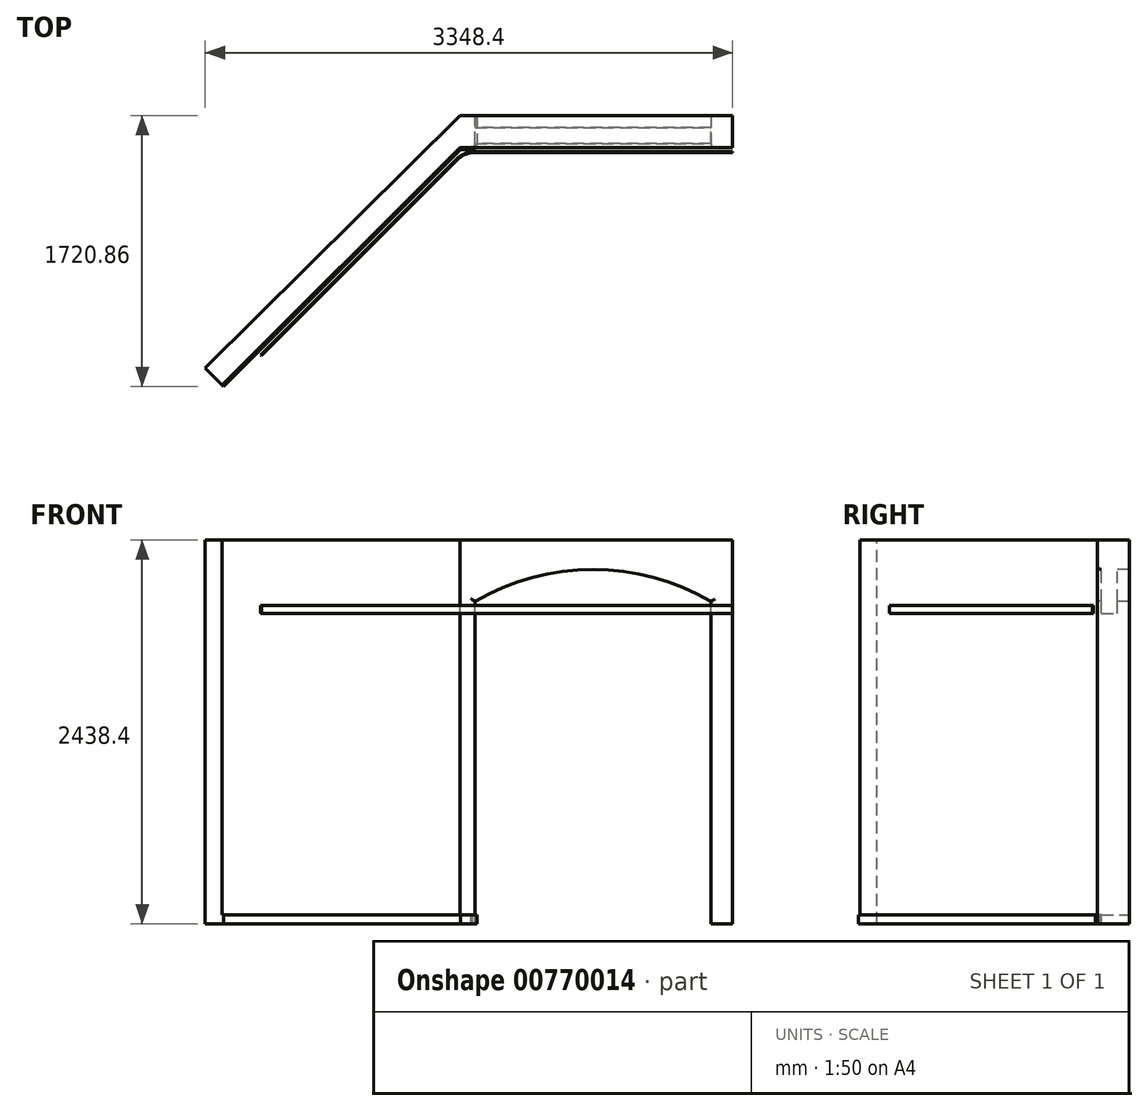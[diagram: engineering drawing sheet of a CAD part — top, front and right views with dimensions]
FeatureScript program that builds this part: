
annotation { "Feature Type Name" : "Feature", "Feature Type Description" : "" }
export const myFeature = defineFeature(function(context is Context, id is Id, definition is map)
    precondition{}
    {
        {
            var Q0;
            Q0=qCreatedBy(makeId("Front.planeOp"),FACE);
            var sketch = newSketch(context, id + "F0", { "sketchPlane" : qUnion([Q0])});
            skLineSegment(sketch, "E0.bottom", {"start": v(0, 0) * mm, "end": v(1498.6, 0) * mm});
            skLineSegment(sketch, "E0.top", {"start": v(0, 1973.26) * mm, "end": v(1498.6, 1973.26) * mm});
            skLineSegment(sketch, "E0.left", {"start": v(0, 0) * mm, "end": v(0, 1973.26) * mm});
            skLineSegment(sketch, "E0.right", {"start": v(1498.6, 0) * mm, "end": v(1498.6, 1973.26) * mm});
            skLineSegment(sketch, "E1", {"start": v(0, 1973.26) * mm, "end": v(0, 2049.46) * mm});
            skLineSegment(sketch, "E2", {"start": v(1498.6, 1973.26) * mm, "end": v(1498.6, 2049.46) * mm});
            skArc(sketch, "E3", {"start": v(1498.6, 2049.46) * mm, "mid": v(749.3, 2251.6) * mm, "end": v(0, 2049.46) * mm});
            skSolve(sketch);
        }
        {
            var Q0;
            Q0=makeQuery(id+"F0.imprint","IMPRINT",FACE,{"disambiguationData":[TD([[makeQuery(id+"F0.imprint","IMPRINT",EDGE,{"derivedFrom":sQuery(id+"F0.wireOp",EDGE,"E0.top")}),1.0]])]});
            extrude(context, id + "F1", {"entities" : qUnion([Q0]), "depth" : 101.6 * mm, "offsetDistance" : 25.4 * mm});
        }
        {
            var Q0;
            Q0=makeQuery(id+"F1.opExtrude","CAP_FACE",FACE,{"disambiguationData":[OSD([sQuery(id+"F0.wireOp",EDGE,"E0.top"),sQuery(id+"F0.wireOp",EDGE,"E1"),sQuery(id+"F0.wireOp",EDGE,"E2"),sQuery(id+"F0.wireOp",EDGE,"E3")])],"isStart":false});
            var sketch = newSketch(context, id + "F2", { "sketchPlane" : qUnion([Q0])});
            skLineSegment(sketch, "E4.bottom", {"start": v(0, 0) * mm, "end": v(1498.6, 0) * mm});
            skLineSegment(sketch, "E4.top", {"start": v(0, 1973.26) * mm, "end": v(1498.6, 1973.26) * mm});
            skLineSegment(sketch, "E4.left", {"start": v(0, 0) * mm, "end": v(0, 1973.26) * mm});
            skLineSegment(sketch, "E4.right", {"start": v(1498.6, 0) * mm, "end": v(1498.6, 1973.26) * mm});
            skLineSegment(sketch, "E5.bottom", {"start": v(-96.84, 0) * mm, "end": v(1635.13, 0) * mm});
            skLineSegment(sketch, "E5.top", {"start": v(-96.84, 2438.4) * mm, "end": v(1635.13, 2438.4) * mm});
            skLineSegment(sketch, "E5.left", {"start": v(-96.84, 0) * mm, "end": v(-96.84, 2438.4) * mm});
            skLineSegment(sketch, "E5.right", {"start": v(1635.13, 0) * mm, "end": v(1635.13, 2438.4) * mm});
            skSolve(sketch);
        }
        {
            var Q0;
            {var subQ3=sQuery(id+"F2.wireOp",EDGE,"E4.left");Q0=makeQuery(id+"F2.imprint","IMPRINT",FACE,{"disambiguationData":[TD([[makeQuery(id+"F2.imprint","IMPRINT",EDGE,{"derivedFrom":subQ3}),1.0]])]});}
            extrude(context, id + "F3", {"entities" : qUnion([Q0]), "oppositeDirection" : true, "depth" : 177.8 * mm, "offsetDistance" : 25.4 * mm});
        }
        {
            var Q0;
            Q0=makeQuery(id+"F3.opExtrude","CAP_FACE",FACE,{"disambiguationData":[OSD([sQuery(id+"F0.wireOp",EDGE,"E1"),sQuery(id+"F0.wireOp",EDGE,"E2"),sQuery(id+"F0.wireOp",EDGE,"E3"),sQuery(id+"F2.wireOp",EDGE,"E4.left"),sQuery(id+"F2.wireOp",EDGE,"E4.right"),sQuery(id+"F2.wireOp",EDGE,"E5.bottom"),sQuery(id+"F2.wireOp",EDGE,"E5.top"),sQuery(id+"F2.wireOp",EDGE,"E5.left"),sQuery(id+"F2.wireOp",EDGE,"E5.right")])],"isStart":true});
            var sketch = newSketch(context, id + "F4", { "sketchPlane" : qUnion([Q0])});
            skSolve(sketch);
        }
        {
            var Q0;
            Q0 = qSketchRegion(id + "F4", true);
            var Q1;
            Q1=makeQuery(id+"F4.imprint","IMPRINT",FACE,{"disambiguationData":[TD([[makeQuery(id+"F4.imprint","IMPRINT",EDGE,{"derivedFrom":makeQuery(id+"F3.opExtrude","CAP_EDGE",EDGE,{"disambiguationData":[OSD([sQuery(id+"F2.wireOp",EDGE,"E5.top")])],"isStart":true})}),-1.0]])]});
            extrude(context, id + "F5", {"entities" : qUnion([Q0, Q1]), "operationType" : NewBodyOperationType.ADD, "depth" : 25.4 * mm, "offsetDistance" : 25.4 * mm});
        }
        {
            var Q0;
            Q0=makeQuery(id+"F5.opExtrude","CAP_EDGE",EDGE,{"disambiguationData":[OSD([sQuery(id+"F0.wireOp",EDGE,"E3")])],"isStart":false});
            var Q1;
            Q1=makeQuery(id+"F5.opExtrude","CAP_EDGE",EDGE,{"disambiguationData":[OSD([sQuery(id+"F0.wireOp",EDGE,"E2"),sQuery(id+"F2.wireOp",EDGE,"E4.right")])],"isStart":false});
            var Q2;
            Q2=makeQuery(id+"F5.opExtrude","CAP_EDGE",EDGE,{"disambiguationData":[OSD([sQuery(id+"F0.wireOp",EDGE,"E1"),sQuery(id+"F2.wireOp",EDGE,"E4.left")])],"isStart":false});
            fillet(context, id + "F6", {"entities" : qUnion([Q0, Q1, Q2]), "radius" : 25.4 * mm, "tangentPropagation" : true, "allowEdgeOverflow" : false});
        }
        {
            var Q0;
            {var subQ0=sQuery(id+"F2.wireOp",EDGE,"E5.top");Q0=makeQuery(id+"F5.boolean.opBoolean","MERGE",FACE,{"derivedFrom":[makeQuery(id+"F3.opExtrude","SWEPT_FACE",FACE,{"disambiguationData":[OSD([subQ0])]}),makeQuery(id+"F5.opExtrude","SWEPT_FACE",FACE,{"disambiguationData":[OSD([subQ0])]})]});}
            var sketch = newSketch(context, id + "F7", { "sketchPlane" : qUnion([Q0])});
            skLineSegment(sketch, "E6", {"start": v(-96.84, -127) * mm, "end": v(-1605.52, -1635.68) * mm});
            skLineSegment(sketch, "E7", {"start": v(-1605.52, -1635.68) * mm, "end": v(-1713.28, -1527.92) * mm});
            skLineSegment(sketch, "E8", {"start": v(-96.84, 76.2) * mm, "end": v(-1713.28, -1527.92) * mm});
            skSolve(sketch);
        }
        {
            var Q0;
            Q0=makeQuery(id+"F7.imprint","IMPRINT",FACE,{"disambiguationData":[TD([[makeQuery(id+"F7.imprint","IMPRINT",EDGE,{"derivedFrom":sQuery(id+"F7.wireOp",EDGE,"E6")}),-1.0]])]});
            extrude(context, id + "F8", {"entities" : qUnion([Q0]), "oppositeDirection" : true, "depth" : 2438.4 * mm, "offsetDistance" : 25.4 * mm});
        }
        {
            var Q0;
            Q0=makeQuery(id+"F8.opExtrude","CAP_FACE",FACE,{"disambiguationData":[OSD([sQuery(id+"F2.wireOp",EDGE,"E5.top"),sQuery(id+"F2.wireOp",EDGE,"E5.left"),sQuery(id+"F7.wireOp",EDGE,"E6"),sQuery(id+"F7.wireOp",EDGE,"E7"),sQuery(id+"F7.wireOp",EDGE,"E8")])],"isStart":false});
            var sketch = newSketch(context, id + "F9", { "sketchPlane" : qUnion([Q0])});
            skLineSegment(sketch, "E9.0", {"start": v(-91.58, 139.7) * mm, "end": v(-1596.54, 1644.66) * mm});
            skLineSegment(sketch, "E9.1", {"start": v(-91.58, 139.7) * mm, "end": v(-25.4, 139.7) * mm});
            skArc(sketch, "E9.2", {"start": v(12.7, 101.6) * mm, "mid": v(1.54, 128.54) * mm, "end": v(-25.4, 139.7) * mm});
            skLineSegment(sketch, "E9.3", {"start": v(12.7, -76.2) * mm, "end": v(12.7, 101.6) * mm});
            skLineSegment(sketch, "E10", {"start": v(12.7, -76.2) * mm, "end": v(0, -76.2) * mm});
            skLineSegment(sketch, "E11", {"start": v(-1596.54, 1644.66) * mm, "end": v(-1605.52, 1635.68) * mm});
            skLineSegment(sketch, "E12", {"start": v(-1605.52, 1635.68) * mm, "end": v(-96.84, 127) * mm});
            skLineSegment(sketch, "E13", {"start": v(-96.84, 127) * mm, "end": v(-20.16, 127) * mm});
            skLineSegment(sketch, "E14", {"start": v(-20.16, 127) * mm, "end": v(0, 106.84) * mm});
            skLineSegment(sketch, "E15", {"start": v(0, 106.84) * mm, "end": v(0, -76.2) * mm});
            skSolve(sketch);
        }
        {
            var Q0;
            Q0=makeQuery(id+"F9.imprint","IMPRINT",FACE,{"disambiguationData":[TD([[makeQuery(id+"F9.imprint","IMPRINT",EDGE,{"derivedFrom":sQuery(id+"F9.wireOp",EDGE,"E9.0")}),1.0]])]});
            extrude(context, id + "F10", {"entities" : qUnion([Q0]), "operationType" : NewBodyOperationType.ADD, "oppositeDirection" : true, "depth" : 57.15 * mm, "offsetDistance" : 25.4 * mm});
        }
        {
            var Q0;
            Q0=makeQuery(id+"F1.opExtrude","SWEPT_FACE",FACE,{"disambiguationData":[OSD([sQuery(id+"F0.wireOp",EDGE,"E0.top")])]});
            var sketch = newSketch(context, id + "F11", { "sketchPlane" : qUnion([Q0])});
            skLineSegment(sketch, "E16", {"start": v(1634.54, 152.4) * mm, "end": v(-5.23, 152.4) * mm});
            skLineSegment(sketch, "E17", {"start": v(-113, 197.04) * mm, "end": v(-1360.57, 1444.61) * mm});
            skPoint(sketch, "E18.visualSharp", {"position": v(-68.36, 152.4) * mm});
            skArc(sketch, "E18.filletArc", {"start": v(-113, 197.04) * mm, "mid": v(-63.55, 164) * mm, "end": v(-5.23, 152.4) * mm});
            skLineSegment(sketch, "E19.0", {"start": v(-108.5, 201.53) * mm, "end": v(-1356.08, 1449.1) * mm});
            skLineSegment(sketch, "E20.0", {"start": v(1634.54, 158.75) * mm, "end": v(-5.23, 158.75) * mm});
            skArc(sketch, "E21.0", {"start": v(-108.5, 201.53) * mm, "mid": v(-61.12, 169.87) * mm, "end": v(-5.23, 158.75) * mm});
            skLineSegment(sketch, "E22", {"start": v(1634.54, 152.4) * mm, "end": v(1634.54, 158.75) * mm});
            skLineSegment(sketch, "E23", {"start": v(-1360.57, 1444.61) * mm, "end": v(-1356.08, 1449.1) * mm});
            skSolve(sketch);
        }
        {
            var Q0;
            Q0=makeQuery(id+"F11.imprint","IMPRINT",FACE,{"disambiguationData":[TD([[makeQuery(id+"F11.imprint","IMPRINT",EDGE,{"derivedFrom":sQuery(id+"F11.wireOp",EDGE,"E16")}),-1.0]])]});
            extrude(context, id + "F12", {"entities" : qUnion([Q0]), "oppositeDirection" : true, "depth" : 50.8 * mm, "offsetDistance" : 25.4 * mm});
        }
    });
